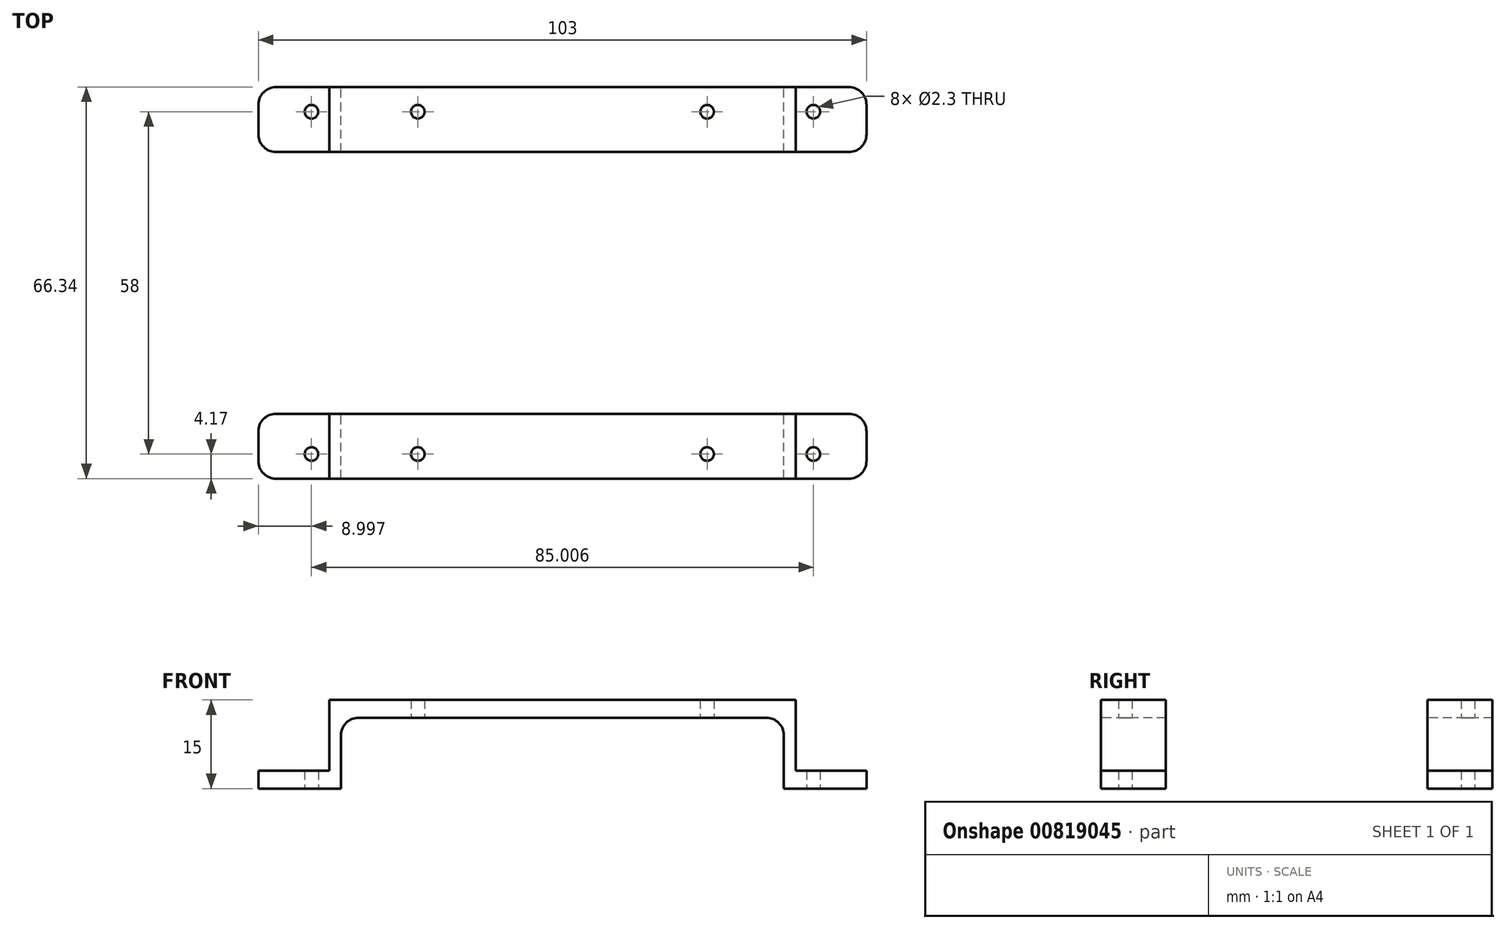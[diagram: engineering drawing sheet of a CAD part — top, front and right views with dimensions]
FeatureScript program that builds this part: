
annotation { "Feature Type Name" : "Feature", "Feature Type Description" : "" }
export const myFeature = defineFeature(function(context is Context, id is Id, definition is map)
    precondition{}
    {
        {
            var Q0;
            Q0=qCreatedBy(makeId("Top.planeOp"),FACE);
            var sketch = newSketch(context, id + "F0", { "sketchPlane" : qUnion([Q0])});
            skLineSegment(sketch, "E0.bottom", {"start": v(-100, -100) * mm, "end": v(100, -100) * mm, "construction": true});
            skLineSegment(sketch, "E0.top", {"start": v(-100, 100) * mm, "end": v(100, 100) * mm, "construction": true});
            skLineSegment(sketch, "E0.left", {"start": v(-100, -100) * mm, "end": v(-100, 100) * mm, "construction": true});
            skLineSegment(sketch, "E0.right", {"start": v(100, -100) * mm, "end": v(100, 100) * mm, "construction": true});
            skPoint(sketch, "E0.middle", {"position": v(0, 0) * mm});
            skCircle(sketch, "E1", {"center": v(-100, 100) * mm, "radius": 2.5 * mm, "construction": true});
            skCircle(sketch, "E2", {"center": v(100, 100) * mm, "radius": 2.5 * mm, "construction": true});
            skCircle(sketch, "E3", {"center": v(100, -100) * mm, "radius": 2.5 * mm, "construction": true});
            skCircle(sketch, "E4", {"center": v(-100, -100) * mm, "radius": 2.5 * mm, "construction": true});
            skLineSegment(sketch, "E5", {"start": v(-100, 100) * mm, "end": v(-77.37, 77.37) * mm, "construction": true});
            skLineSegment(sketch, "E6", {"start": v(-77.37, 77.37) * mm, "end": v(-67.47, 67.47) * mm, "construction": true});
            skCircle(sketch, "E7", {"center": v(-77.37, 77.37) * mm, "radius": 2.25 * mm});
            skCircle(sketch, "E8", {"center": v(-67.47, 67.47) * mm, "radius": 2.25 * mm});
            skLineSegment(sketch, "E9.bottom", {"start": v(-85, 85) * mm, "end": v(85, 85) * mm});
            skLineSegment(sketch, "E9.top", {"start": v(-85, -85) * mm, "end": v(85, -85) * mm});
            skLineSegment(sketch, "E9.left", {"start": v(-85, 85) * mm, "end": v(-85, -85) * mm});
            skLineSegment(sketch, "E9.right", {"start": v(85, 85) * mm, "end": v(85, -85) * mm});
            skLineSegment(sketch, "E10.bottom", {"start": v(-30.75, 2.54) * mm, "end": v(30.75, 2.54) * mm, "construction": true});
            skLineSegment(sketch, "E10.top", {"start": v(-30.75, 79.04) * mm, "end": v(30.75, 79.04) * mm, "construction": true});
            skLineSegment(sketch, "E10.left", {"start": v(-30.75, 2.54) * mm, "end": v(-30.75, 79.04) * mm, "construction": true});
            skLineSegment(sketch, "E10.right", {"start": v(30.75, 2.54) * mm, "end": v(30.75, 79.04) * mm, "construction": true});
            skPoint(sketch, "E10.middle", {"position": v(0, 40.8) * mm});
            skLineSegment(sketch, "E11.bottom", {"start": v(-35, -9.2) * mm, "end": v(35, -9.2) * mm, "construction": true});
            skLineSegment(sketch, "E11.top", {"start": v(-35, 90.8) * mm, "end": v(35, 90.8) * mm, "construction": true});
            skLineSegment(sketch, "E11.left", {"start": v(-35, -9.2) * mm, "end": v(-35, 90.8) * mm, "construction": true});
            skLineSegment(sketch, "E11.right", {"start": v(35, -9.2) * mm, "end": v(35, 90.8) * mm, "construction": true});
            skLineSegment(sketch, "E12.bottom", {"start": v(24.5, 22.83) * mm, "end": v(-24.5, 22.83) * mm, "construction": true});
            skLineSegment(sketch, "E12.top", {"start": v(24.5, 80.83) * mm, "end": v(-24.5, 80.83) * mm, "construction": true});
            skLineSegment(sketch, "E12.left", {"start": v(24.5, 22.83) * mm, "end": v(24.5, 80.83) * mm, "construction": true});
            skLineSegment(sketch, "E12.right", {"start": v(-24.5, 22.83) * mm, "end": v(-24.5, 80.83) * mm, "construction": true});
            skPoint(sketch, "E12.middle", {"position": v(0, 51.83) * mm});
            skLineSegment(sketch, "E13.bottom", {"start": v(28, 96.83) * mm, "end": v(-28, 96.83) * mm, "construction": true});
            skLineSegment(sketch, "E13.top", {"start": v(28, 6.83) * mm, "end": v(-28, 6.83) * mm, "construction": true});
            skLineSegment(sketch, "E13.left", {"start": v(28, 96.83) * mm, "end": v(28, 6.83) * mm, "construction": true});
            skLineSegment(sketch, "E13.right", {"start": v(-28, 96.83) * mm, "end": v(-28, 6.83) * mm, "construction": true});
            skLineSegment(sketch, "E14", {"start": v(0, 0) * mm, "end": v(0, 19) * mm, "construction": true});
            skLineSegment(sketch, "E15", {"start": v(0, 0) * mm, "end": v(16.24, 0) * mm, "construction": true});
            skCircle(sketch, "E16.MirrorC", {"center": v(77.37, 77.37) * mm, "radius": 2.25 * mm});
            skCircle(sketch, "E17.MirrorC", {"center": v(67.47, 67.47) * mm, "radius": 2.25 * mm});
            skCircle(sketch, "E18.MirrorC", {"center": v(-67.47, -67.47) * mm, "radius": 2.25 * mm});
            skCircle(sketch, "E19.MirrorC", {"center": v(-77.37, -77.37) * mm, "radius": 2.25 * mm});
            skCircle(sketch, "E20.MirrorC", {"center": v(77.37, -77.37) * mm, "radius": 2.25 * mm});
            skCircle(sketch, "E21.MirrorC", {"center": v(67.47, -67.47) * mm, "radius": 2.25 * mm});
            skCircle(sketch, "E22", {"center": v(-24.5, 80.83) * mm, "radius": 1.15 * mm});
            skCircle(sketch, "E23", {"center": v(24.5, 80.83) * mm, "radius": 1.15 * mm});
            skCircle(sketch, "E24", {"center": v(24.5, 22.83) * mm, "radius": 1.15 * mm});
            skCircle(sketch, "E25", {"center": v(-24.5, 22.83) * mm, "radius": 1.15 * mm});
            skCircle(sketch, "E26", {"center": v(-30.75, 79.04) * mm, "radius": 1.15 * mm});
            skCircle(sketch, "E27", {"center": v(30.75, 79.04) * mm, "radius": 1.15 * mm});
            skCircle(sketch, "E28", {"center": v(30.75, 2.54) * mm, "radius": 1.15 * mm});
            skCircle(sketch, "E29", {"center": v(-30.75, 2.54) * mm, "radius": 1.15 * mm});
            skLineSegment(sketch, "E30.bottom", {"start": v(-67.5, 53.5) * mm, "end": v(67.5, 53.5) * mm, "construction": true});
            skLineSegment(sketch, "E30.top", {"start": v(-67.5, -53.5) * mm, "end": v(67.5, -53.5) * mm, "construction": true});
            skLineSegment(sketch, "E30.left", {"start": v(-67.5, 53.5) * mm, "end": v(-67.5, -53.5) * mm, "construction": true});
            skLineSegment(sketch, "E30.right", {"start": v(67.5, 53.5) * mm, "end": v(67.5, -53.5) * mm, "construction": true});
            skCircle(sketch, "E31", {"center": v(-67.5, 53.5) * mm, "radius": 1.25 * mm});
            skCircle(sketch, "E32", {"center": v(67.5, 53.5) * mm, "radius": 1.25 * mm});
            skCircle(sketch, "E33", {"center": v(67.5, -53.5) * mm, "radius": 1.25 * mm});
            skCircle(sketch, "E34", {"center": v(-67.5, -53.5) * mm, "radius": 1.25 * mm});
            skLineSegment(sketch, "E35.bottom", {"start": v(-42.5, 22.83) * mm, "end": v(42.5, 22.83) * mm, "construction": true});
            skLineSegment(sketch, "E35.top", {"start": v(-42.5, 80.83) * mm, "end": v(42.5, 80.83) * mm, "construction": true});
            skLineSegment(sketch, "E35.left", {"start": v(-42.5, 22.83) * mm, "end": v(-42.5, 80.83) * mm, "construction": true});
            skLineSegment(sketch, "E35.right", {"start": v(42.5, 22.83) * mm, "end": v(42.5, 80.83) * mm, "construction": true});
            skCircle(sketch, "E36", {"center": v(-42.5, 80.83) * mm, "radius": 1.15 * mm});
            skCircle(sketch, "E37", {"center": v(-42.5, 22.83) * mm, "radius": 1.15 * mm});
            skCircle(sketch, "E38", {"center": v(42.5, 22.83) * mm, "radius": 1.15 * mm});
            skCircle(sketch, "E39", {"center": v(42.5, 80.83) * mm, "radius": 1.15 * mm});
            skLineSegment(sketch, "E40.bottom", {"start": v(-51.5, 85) * mm, "end": v(51.5, 85) * mm});
            skLineSegment(sketch, "E40.top", {"start": v(-51.5, 18.66) * mm, "end": v(51.5, 18.66) * mm});
            skLineSegment(sketch, "E40.left", {"start": v(-51.5, 85) * mm, "end": v(-51.5, 18.66) * mm});
            skLineSegment(sketch, "E40.right", {"start": v(51.5, 85) * mm, "end": v(51.5, 18.66) * mm});
            skLineSegment(sketch, "E41.bottom", {"start": v(-51.5, 74) * mm, "end": v(51.5, 74) * mm});
            skLineSegment(sketch, "E41.top", {"start": v(-51.5, 29.66) * mm, "end": v(51.5, 29.66) * mm});
            skLineSegment(sketch, "E41.left", {"start": v(-51.5, 74) * mm, "end": v(-51.5, 29.66) * mm});
            skLineSegment(sketch, "E41.right", {"start": v(51.5, 74) * mm, "end": v(51.5, 29.66) * mm});
            skSolve(sketch);
        }
        {
            var Q0;
            Q0=makeQuery(id+"F0.imprint","IMPRINT",FACE,{"disambiguationData":[TD([[makeQuery(id+"F0.imprint","IMPRINT",EDGE,{"derivedFrom":sQuery(id+"F0.wireOp",EDGE,"E22")}),-1.0]])]});
            var Q1;
            Q1=makeQuery(id+"F0.imprint","IMPRINT",FACE,{"disambiguationData":[TD([[makeQuery(id+"F0.imprint","IMPRINT",EDGE,{"derivedFrom":sQuery(id+"F0.wireOp",EDGE,"E24")}),-1.0]])]});
            var Q2;
            Q2=makeQuery(id+"F0.imprint","IMPRINT",FACE,{"disambiguationData":[TD([[makeQuery(id+"F0.imprint","IMPRINT",EDGE,{"derivedFrom":sQuery(id+"F0.wireOp",EDGE,"E26")}),1.0]])]});
            var Q3;
            Q3=makeQuery(id+"F0.imprint","IMPRINT",FACE,{"disambiguationData":[TD([[makeQuery(id+"F0.imprint","IMPRINT",EDGE,{"derivedFrom":sQuery(id+"F0.wireOp",EDGE,"E27")}),1.0]])]});
            extrude(context, id + "F1", {"entities" : qUnion([Q0, Q1, Q2, Q3]), "depth" : 15 * mm, "offsetDistance" : 25 * mm});
        }
        {
            var Q0;
            Q0=qCreatedBy(makeId("Front.planeOp"),FACE);
            var sketch = newSketch(context, id + "F2", { "sketchPlane" : qUnion([Q0])});
            skLineSegment(sketch, "E42.bottom", {"start": v(37.5, -12) * mm, "end": v(-37.5, -12) * mm});
            skLineSegment(sketch, "E42.top", {"start": v(37.5, 12) * mm, "end": v(-37.5, 12) * mm});
            skLineSegment(sketch, "E42.left", {"start": v(37.5, -12) * mm, "end": v(37.5, 12) * mm});
            skLineSegment(sketch, "E42.right", {"start": v(-37.5, -12) * mm, "end": v(-37.5, 12) * mm});
            skPoint(sketch, "E42.middle", {"position": v(0, 0) * mm});
            skLineSegment(sketch, "E43", {"start": v(0, 0) * mm, "end": v(-51.5, 0) * mm, "construction": true});
            skLineSegment(sketch, "E44", {"start": v(-51.5, 0) * mm, "end": v(-51.5, 15) * mm, "construction": true});
            skLineSegment(sketch, "E45.bottom", {"start": v(-51.5, 15) * mm, "end": v(-39.5, 15) * mm});
            skLineSegment(sketch, "E45.top", {"start": v(-51.5, 3) * mm, "end": v(-39.5, 3) * mm});
            skLineSegment(sketch, "E45.left", {"start": v(-51.5, 15) * mm, "end": v(-51.5, 3) * mm});
            skLineSegment(sketch, "E45.right", {"start": v(-39.5, 15) * mm, "end": v(-39.5, 3) * mm});
            skLineSegment(sketch, "E46", {"start": v(0, 0) * mm, "end": v(0, 5.25) * mm, "construction": true});
            skLineSegment(sketch, "E47.MirrorCS", {"start": v(39.5, 15) * mm, "end": v(39.5, 3) * mm});
            skLineSegment(sketch, "E48.MirrorCS", {"start": v(51.5, 15) * mm, "end": v(39.5, 15) * mm});
            skLineSegment(sketch, "E49.MirrorCS", {"start": v(51.5, 15) * mm, "end": v(51.5, 3) * mm});
            skLineSegment(sketch, "E50.MirrorCS", {"start": v(51.5, 3) * mm, "end": v(39.5, 3) * mm});
            skLineSegment(sketch, "E51.MirrorCS", {"start": v(51.5, 0) * mm, "end": v(51.5, 15) * mm, "construction": true});
            skSolve(sketch);
        }
        {
            var Q0;
            Q0 = qSketchRegion(id + "F2", true);
            extrude(context, id + "F3", {"entities" : qUnion([Q0]), "operationType" : NewBodyOperationType.REMOVE, "endBound" : BoundingType.THROUGH_ALL, "oppositeDirection" : true, "depth" : 25 * mm, "offsetDistance" : 25 * mm});
        }
        {
            var Q0;
            {var subQ0=sQuery(id+"F2.wireOp",EDGE,"E45.right");Q0=makeQuery(id+"F3.boolean.opBoolean","COPY",EDGE,{"disambiguationData":[topologyDisambiguationEdgeConnected([makeQuery(id+"F1.opExtrude","CAP_FACE",FACE,{"disambiguationData":[OSD([sQuery(id+"F0.wireOp",EDGE,"E24"),sQuery(id+"F0.wireOp",EDGE,"E25"),sQuery(id+"F0.wireOp",EDGE,"E37"),sQuery(id+"F0.wireOp",EDGE,"E38"),sQuery(id+"F0.wireOp",EDGE,"E40.top"),sQuery(id+"F0.wireOp",EDGE,"E40.left"),sQuery(id+"F0.wireOp",EDGE,"E40.right"),sQuery(id+"F0.wireOp",EDGE,"E41.top")])],"isStart":false})])],"derivedFrom":makeQuery(id+"F3.opExtrude","SWEPT_EDGE",EDGE,{"disambiguationData":[OSD([sQuery(id+"F2.wireOp",EDGE,"E45.bottom"),subQ0])]})});}
            var Q1;
            {var subQ0=sQuery(id+"F2.wireOp",EDGE,"E42.right");var subQ1=sQuery(id+"F2.wireOp",EDGE,"E42.top");Q1=makeQuery(id+"F3.boolean.opBoolean","COPY",EDGE,{"disambiguationData":[TD([makeQuery(id+"F1.opExtrude","SWEPT_FACE",FACE,{"disambiguationData":[OSD([sQuery(id+"F0.wireOp",EDGE,"E40.top")])]})])],"derivedFrom":makeQuery(id+"F3.opExtrude","SWEPT_EDGE",EDGE,{"disambiguationData":[OSD([subQ1,subQ0])]})});}
            var Q2;
            {var subQ0=sQuery(id+"F2.wireOp",EDGE,"E42.right");var subQ1=sQuery(id+"F2.wireOp",EDGE,"E42.top");Q2=makeQuery(id+"F3.boolean.opBoolean","COPY",EDGE,{"disambiguationData":[TD([makeQuery(id+"F1.opExtrude","SWEPT_FACE",FACE,{"disambiguationData":[OSD([sQuery(id+"F0.wireOp",EDGE,"E9.bottom")])]})])],"derivedFrom":makeQuery(id+"F3.opExtrude","SWEPT_EDGE",EDGE,{"disambiguationData":[OSD([subQ1,subQ0])]})});}
            var Q3;
            Q3=makeQuery(id+"F1.opExtrude","SWEPT_EDGE",EDGE,{"disambiguationData":[OSD([sQuery(id+"F0.wireOp",EDGE,"E40.top"),sQuery(id+"F0.wireOp",EDGE,"E40.left")])]});
            var Q4;
            Q4=makeQuery(id+"F1.opExtrude","SWEPT_EDGE",EDGE,{"disambiguationData":[OSD([sQuery(id+"F0.wireOp",EDGE,"E40.left"),sQuery(id+"F0.wireOp",EDGE,"E41.top")])]});
            var Q5;
            Q5=makeQuery(id+"F1.opExtrude","SWEPT_EDGE",EDGE,{"disambiguationData":[OSD([sQuery(id+"F0.wireOp",EDGE,"E40.left"),sQuery(id+"F0.wireOp",EDGE,"E41.bottom")])]});
            var Q6;
            Q6=makeQuery(id+"F1.opExtrude","SWEPT_EDGE",EDGE,{"disambiguationData":[OSD([sQuery(id+"F0.wireOp",EDGE,"E9.bottom"),sQuery(id+"F0.wireOp",EDGE,"E40.left")])]});
            var Q7;
            {var subQ0=sQuery(id+"F2.wireOp",EDGE,"E45.right");Q7=makeQuery(id+"F3.boolean.opBoolean","COPY",EDGE,{"disambiguationData":[topologyDisambiguationEdgeConnected([makeQuery(id+"F1.opExtrude","CAP_FACE",FACE,{"disambiguationData":[OSD([sQuery(id+"F0.wireOp",EDGE,"E9.bottom"),sQuery(id+"F0.wireOp",EDGE,"E22"),sQuery(id+"F0.wireOp",EDGE,"E23"),sQuery(id+"F0.wireOp",EDGE,"E36"),sQuery(id+"F0.wireOp",EDGE,"E39"),sQuery(id+"F0.wireOp",EDGE,"E40.left"),sQuery(id+"F0.wireOp",EDGE,"E40.right"),sQuery(id+"F0.wireOp",EDGE,"E41.bottom")])],"isStart":false})])],"derivedFrom":makeQuery(id+"F3.opExtrude","SWEPT_EDGE",EDGE,{"disambiguationData":[OSD([sQuery(id+"F2.wireOp",EDGE,"E45.bottom"),subQ0])]})});}
            var Q8;
            {var subQ0=sQuery(id+"F2.wireOp",EDGE,"E47.MirrorCS");Q8=makeQuery(id+"F3.boolean.opBoolean","COPY",EDGE,{"disambiguationData":[topologyDisambiguationEdgeConnected([makeQuery(id+"F1.opExtrude","CAP_FACE",FACE,{"disambiguationData":[OSD([sQuery(id+"F0.wireOp",EDGE,"E24"),sQuery(id+"F0.wireOp",EDGE,"E25"),sQuery(id+"F0.wireOp",EDGE,"E37"),sQuery(id+"F0.wireOp",EDGE,"E38"),sQuery(id+"F0.wireOp",EDGE,"E40.top"),sQuery(id+"F0.wireOp",EDGE,"E40.left"),sQuery(id+"F0.wireOp",EDGE,"E40.right"),sQuery(id+"F0.wireOp",EDGE,"E41.top")])],"isStart":false})])],"derivedFrom":makeQuery(id+"F3.opExtrude","SWEPT_EDGE",EDGE,{"disambiguationData":[OSD([subQ0,sQuery(id+"F2.wireOp",EDGE,"E48.MirrorCS")])]})});}
            var Q9;
            Q9=makeQuery(id+"F1.opExtrude","SWEPT_EDGE",EDGE,{"disambiguationData":[OSD([sQuery(id+"F0.wireOp",EDGE,"E40.top"),sQuery(id+"F0.wireOp",EDGE,"E40.right")])]});
            var Q10;
            Q10=makeQuery(id+"F1.opExtrude","SWEPT_EDGE",EDGE,{"disambiguationData":[OSD([sQuery(id+"F0.wireOp",EDGE,"E40.right"),sQuery(id+"F0.wireOp",EDGE,"E41.top")])]});
            var Q11;
            {var subQ0=sQuery(id+"F2.wireOp",EDGE,"E47.MirrorCS");Q11=makeQuery(id+"F3.boolean.opBoolean","COPY",EDGE,{"disambiguationData":[topologyDisambiguationEdgeConnected([makeQuery(id+"F1.opExtrude","CAP_FACE",FACE,{"disambiguationData":[OSD([sQuery(id+"F0.wireOp",EDGE,"E9.bottom"),sQuery(id+"F0.wireOp",EDGE,"E22"),sQuery(id+"F0.wireOp",EDGE,"E23"),sQuery(id+"F0.wireOp",EDGE,"E36"),sQuery(id+"F0.wireOp",EDGE,"E39"),sQuery(id+"F0.wireOp",EDGE,"E40.left"),sQuery(id+"F0.wireOp",EDGE,"E40.right"),sQuery(id+"F0.wireOp",EDGE,"E41.bottom")])],"isStart":false})])],"derivedFrom":makeQuery(id+"F3.opExtrude","SWEPT_EDGE",EDGE,{"disambiguationData":[OSD([subQ0,sQuery(id+"F2.wireOp",EDGE,"E48.MirrorCS")])]})});}
            var Q12;
            Q12=makeQuery(id+"F1.opExtrude","SWEPT_EDGE",EDGE,{"disambiguationData":[OSD([sQuery(id+"F0.wireOp",EDGE,"E40.right"),sQuery(id+"F0.wireOp",EDGE,"E41.bottom")])]});
            var Q13;
            Q13=makeQuery(id+"F1.opExtrude","SWEPT_EDGE",EDGE,{"disambiguationData":[OSD([sQuery(id+"F0.wireOp",EDGE,"E9.bottom"),sQuery(id+"F0.wireOp",EDGE,"E40.right")])]});
            var Q14;
            {var subQ0=sQuery(id+"F2.wireOp",EDGE,"E42.top");var subQ1=sQuery(id+"F2.wireOp",EDGE,"E42.left");Q14=makeQuery(id+"F3.boolean.opBoolean","COPY",EDGE,{"disambiguationData":[TD([makeQuery(id+"F1.opExtrude","SWEPT_FACE",FACE,{"disambiguationData":[OSD([sQuery(id+"F0.wireOp",EDGE,"E40.top")])]})])],"derivedFrom":makeQuery(id+"F3.opExtrude","SWEPT_EDGE",EDGE,{"disambiguationData":[OSD([subQ0,subQ1])]})});}
            var Q15;
            {var subQ0=sQuery(id+"F2.wireOp",EDGE,"E42.top");var subQ1=sQuery(id+"F2.wireOp",EDGE,"E42.left");Q15=makeQuery(id+"F3.boolean.opBoolean","COPY",EDGE,{"disambiguationData":[TD([makeQuery(id+"F1.opExtrude","SWEPT_FACE",FACE,{"disambiguationData":[OSD([sQuery(id+"F0.wireOp",EDGE,"E9.bottom")])]})])],"derivedFrom":makeQuery(id+"F3.opExtrude","SWEPT_EDGE",EDGE,{"disambiguationData":[OSD([subQ0,subQ1])]})});}
            fillet(context, id + "F4", {"entities" : qUnion([Q0, Q1, Q2, Q3, Q4, Q5, Q6, Q7, Q8, Q9, Q10, Q11, Q12, Q13, Q14, Q15]), "radius" : 3 * mm, "tangentPropagation" : true, "allowEdgeOverflow" : false});
        }
    });
